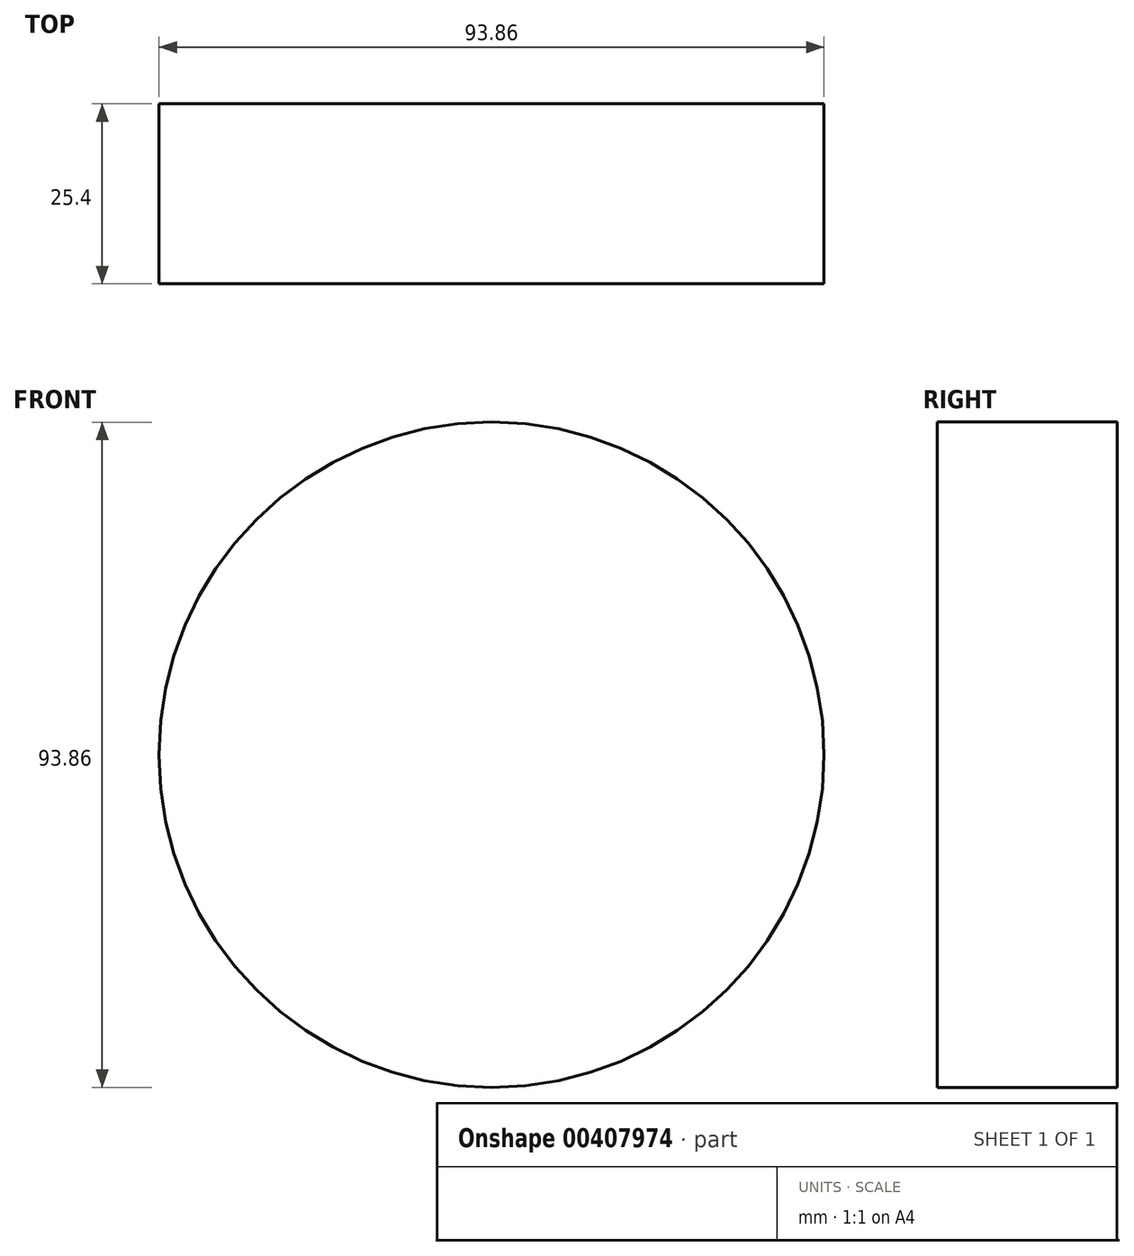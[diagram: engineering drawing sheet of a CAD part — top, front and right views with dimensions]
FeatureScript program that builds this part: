
annotation { "Feature Type Name" : "Feature", "Feature Type Description" : "" }
export const myFeature = defineFeature(function(context is Context, id is Id, definition is map)
    precondition{}
    {
        {
            var Q0;
            Q0=qCreatedBy(makeId("Front.planeOp"),FACE);
            var sketch = newSketch(context, id + "F0", { "sketchPlane" : qUnion([Q0])});
            skCircle(sketch, "E0", {"center": v(0, 0) * mm, "radius": 46.93 * mm});
            skSolve(sketch);
        }
        {
            var Q0;
            Q0=makeQuery(id+"F0.imprint","IMPRINT",FACE,{"disambiguationData":[TD([[makeQuery(id+"F0.imprint","IMPRINT",EDGE,{"derivedFrom":sQuery(id+"F0.wireOp",EDGE,"E0")}),1.0]])]});
            extrude(context, id + "F1", {"entities" : qUnion([Q0]), "depth" : 25.4 * mm});
        }
    });
